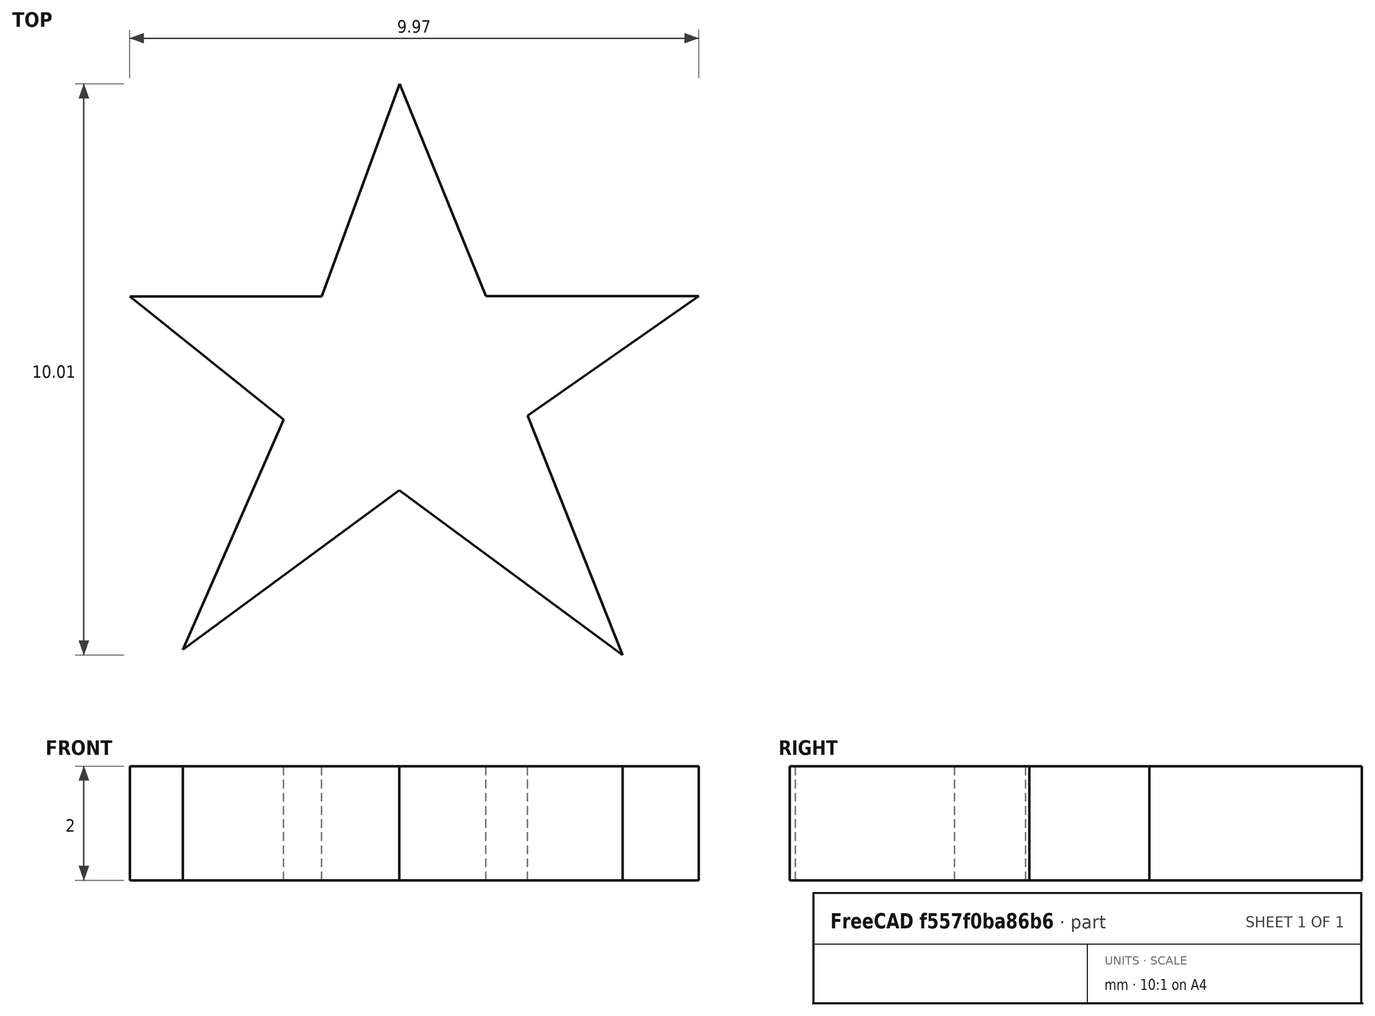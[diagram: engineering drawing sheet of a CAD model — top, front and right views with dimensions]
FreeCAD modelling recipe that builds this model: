
FCSTD DOCUMENT  (FreeCAD 0.14R3702 (Git))
Label: etoile10
License: CC-BY 3.0
LicenseURL: http://creativecommons.org/licenses/by/3.0/
objects: Sketcher::SketchObject×1, PartDesign::Pad×1
note: 3 computed .brp shape members not serialized (recipe doc carries the construction recipe); baked Part::Feature solids carry a one-line shape summary decoded from their .brp

FEATURE [Sketcher::SketchObject] Sketch
  sketch-geometry (10):
    g0: LineSegment StartX=10.0443 StartY=-13.7588 StartZ=0 EndX=13.4064 EndY=-13.7588 EndZ=0
    g1: LineSegment StartX=13.4064 StartY=-13.7588 StartZ=0 EndX=14.7706 EndY=-10.0267 EndZ=0
    g2: LineSegment StartX=14.7706 StartY=-10.0267 StartZ=0 EndX=16.2806 EndY=-13.7486 EndZ=0
    g3: LineSegment StartX=16.2806 StartY=-13.7486 StartZ=0 EndX=20.0066 EndY=-13.7486 EndZ=0
    g4: LineSegment StartX=20.0066 StartY=-13.7486 StartZ=0 EndX=17.0113 EndY=-15.8473 EndZ=0
    g5: LineSegment StartX=17.0113 StartY=-15.8473 StartZ=0 EndX=18.6726 EndY=-20.0439 EndZ=0
    g6: LineSegment StartX=18.6726 StartY=-20.0439 StartZ=0 EndX=14.7655 EndY=-17.156 EndZ=0
    g7: LineSegment StartX=14.7655 StartY=-17.156 StartZ=0 EndX=10.9742 EndY=-19.9461 EndZ=0
    g8: LineSegment StartX=10.9742 StartY=-19.9461 StartZ=0 EndX=12.7375 EndY=-15.9124 EndZ=0
    g9: LineSegment StartX=12.7375 StartY=-15.9124 StartZ=0 EndX=10.0443 EndY=-13.7588 EndZ=0
  constraints (12):
    c: Horizontal(g0)
    c: Coincident(g0,g1)
    c: Coincident(g1,g2)
    c: Coincident(g2,g3)
    c: Horizontal(g3)
    c: Coincident(g3,g4)
    c: Coincident(g4,g5)
    c: Coincident(g5,g6)
    c: Coincident(g6,g7)
    c: Coincident(g7,g8)
    c: Coincident(g8,g9)
    c: Coincident(g9,g0)
FEATURE [PartDesign::Pad] Pad
  Length = 2
  Length2 = 100
  Sketch = -> Sketch
  Type = 0
